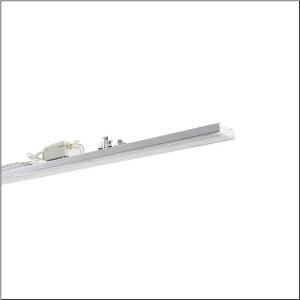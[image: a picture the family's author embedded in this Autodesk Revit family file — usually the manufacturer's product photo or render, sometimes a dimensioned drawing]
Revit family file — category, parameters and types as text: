
# Revit family: licross_r__21_recessed_ho_52tl12de475m_fe62
name_source: partatom
category: Lighting Fixtures
units: mm (PartAtom-declared; Revit-internal decimal feet)

## family parameters
Cut with Voids When Loaded = No
Host = Face
Light Source = No
Part Type = Normal
Room Calculation Point = No
Round Connector Dimension = Use Diameter
Shared = No

## types (1)
- --- (1 x LED, 7500 lm, 44.1 W, 4000K)
    Apparent Load = 44 VA
    CIE Flux Codes = 69 91 98 100 100
    Color Rendering = 80
    Color Temperature = 4000K
    Default Elevation = 1800 mm
    Description = Licross® 21 Recessed HO, luminaire insert, of sheet steel, galvanised, coil coated, white, length: 750mm, width: 66mm, height: 67mm, LED rated luminous flux: 7.500lm, light colour: 840, control gear: DALI 2, with plug, 5-pole, with phase selection, mains connection: 220..240V, AC, 50/60Hz, rated input power: 44W, halogen-free wiring, primary light control with lens, of plastic, primary optical cover: cover, of PMMA, light emission: direct distribution, primary light characteristic: symmetric, protection rating (complete): IP40, insulation class (complete): insulation class I (protective earthing), certification: CE, ENEC, VDE, UKCA, protection symbol: D if used in an environment without relevant dust loads with corresponding accessories, impact resistance: IK06, permissible ambient temperature for indoor applications: -25..+30°C, corresponds to IFS (International Featured Standards) requirements for safety and quality in the food industry, reducing of maximum allowable ambient temperature of 5°C with ceiling mounting, LABS conformity tested according to VDMA 24364:2018-05, packaging unit: 1 piece
    Height = 58 mm
    Lamp = 1 x LED
    Lamp Light Flux = 7500 lm
    Lamp Power = 44.1 W
    Lamp count = 1
    Length = 750 mm
    Luminous efficacy = 170 lm/W
    Manufacturer = Siteco
    ModVariant = No
    Model = 52TL12DE475M
    Mounting Place = Ceiling
    Mounting Type = Pendant
    Number of Poles = 1
    OnlyDefault = Yes
    Power Factor = 1
    Product Name = Licross® 21 Recessed HO
    Product group = luminaire insert
    ProductGroupID = 901
    Protection Class = Protection class I
    Protection Degree = IP 40
    RLX_Detail_Level = 1
    RLX_Emergency_Light_Flux = 0 lm
    RLX_Emergency_Type = 0
    RLX_Emergency_Type_DB = No
    RlxData = <blob elided: 29569 chars, md5=ae2591b2>
    Socket = socket
    Standby Power = 0 W
    System Light Flux = 7500 lm
    System Power = 44 W
    Type Comments = factory setting: luminous flux: 100 % | dim-lin: 254 | 484 mA
    Type Image = l_1296930.jpg
    URL = http://relux.com
    VarID = @adj_046807
    Voltage = 0 V
    Weight = 0.00 kg
    Width = 66 mm

## geometry (parser evidence)
native form markers: Blend x4, Sweep x9
no freeform markers — native parametric forms only
